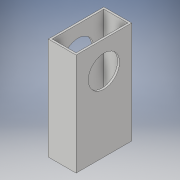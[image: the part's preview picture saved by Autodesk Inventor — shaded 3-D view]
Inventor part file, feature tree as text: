
AUTODESK INVENTOR PART (.ipt)
format: ipt  version: 2018 (Build 220112000, 112)  size: 111,616 bytes
history: native  units: in
note: dims shown in document units (in); Inventor stores cm internally (conversion verified against a paired STEP export)
features: extrude x2, sketch x2
ambient origin geometry x8: Origin, YZ Plane, XZ Plane, XY Plane, X Axis, Y Axis, Z Axis, Center Point
bodies: Solid1 (feature_tree)
feature tree (4):
  extrude  "Extrusion1"  Depth=2.0in
  extrude  "Extrusion2"  Depth=3.675in TaperAngle=0.0deg
  sketch  "Sketch2"  dims[d0=1.0in d1=2.0in]
  sketch  "Sketch3"  dims[d2=0.07in d3=3.675in d4=0.0in d5=1.675in d6=1.0in d7=1.125in d8=1.675in d9=0.0in]
